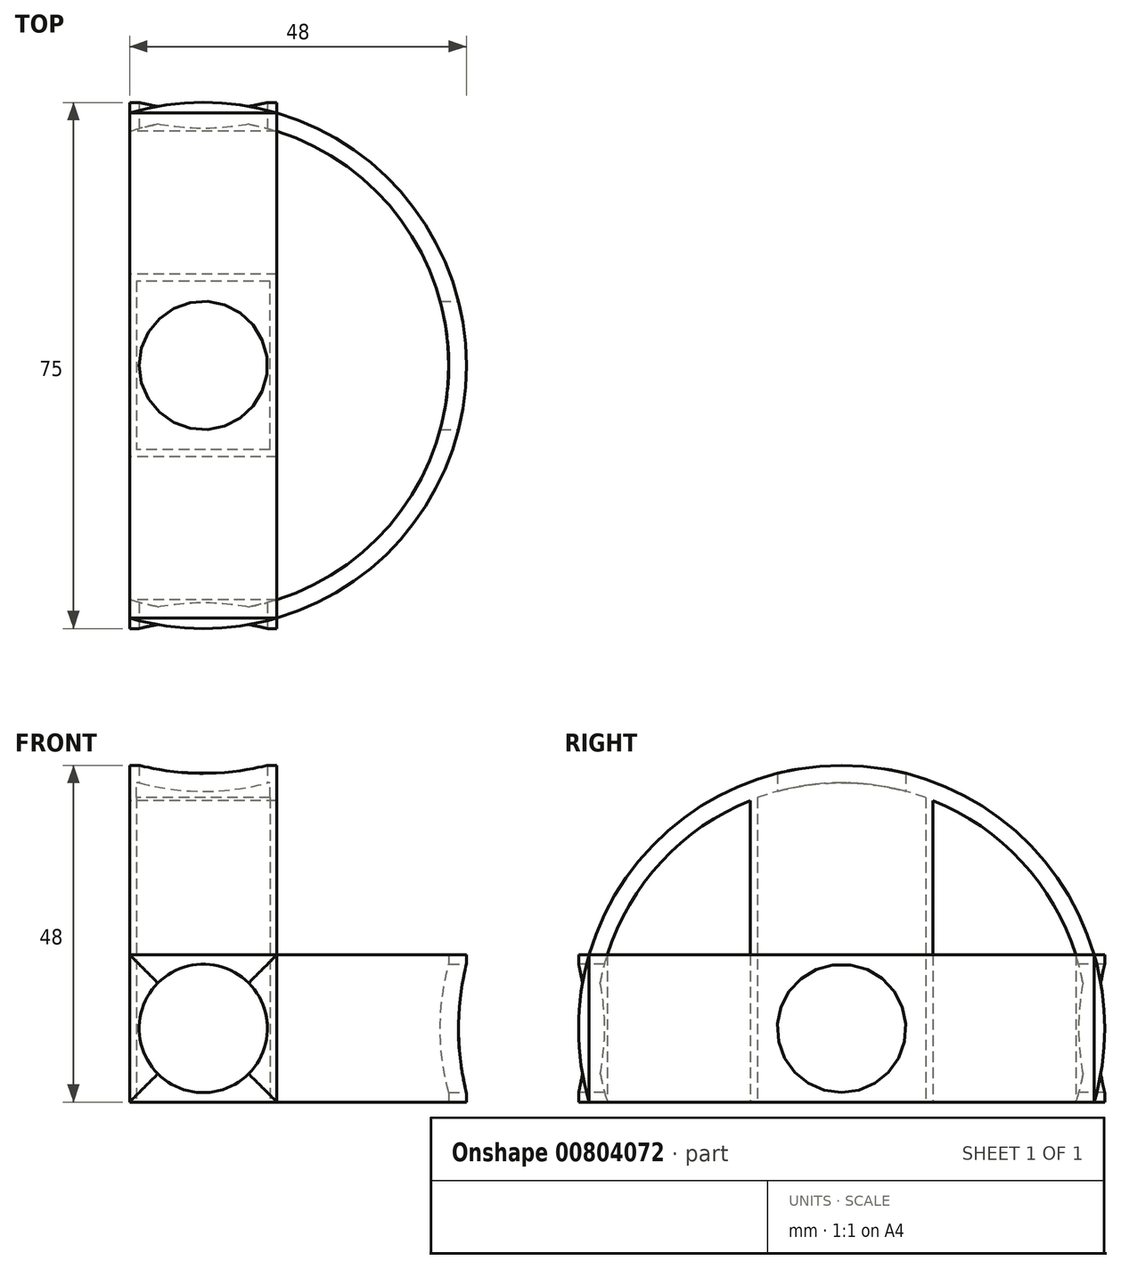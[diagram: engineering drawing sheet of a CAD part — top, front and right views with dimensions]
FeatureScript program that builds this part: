
annotation { "Feature Type Name" : "Feature", "Feature Type Description" : "" }
export const myFeature = defineFeature(function(context is Context, id is Id, definition is map)
    precondition{}
    {
        {
            var Q0;
            Q0=qCreatedBy(makeId("Top.planeOp"),FACE);
            var sketch = newSketch(context, id + "F0", { "sketchPlane" : qUnion([Q0])});
            skCircle(sketch, "E0", {"center": v(0, 0) * mm, "radius": 37.5 * mm});
            skCircle(sketch, "E1", {"center": v(0, 0) * mm, "radius": 35 * mm});
            skSolve(sketch);
        }
        {
            var Q0;
            Q0 = qSketchRegion(id + "F0", true);
            extrude(context, id + "F1", {"entities" : qUnion([Q0]), "endBound" : BoundingType.SYMMETRIC, "depth" : 21 * mm, "offsetDistance" : 25 * mm});
        }
        {
            var Q0;
            Q0=qCreatedBy(makeId("Right.planeOp"),FACE);
            var sketch = newSketch(context, id + "F2", { "sketchPlane" : qUnion([Q0])});
            skCircle(sketch, "E2", {"center": v(0, 0) * mm, "radius": 9.15 * mm});
            skSolve(sketch);
        }
        {
            var Q0;
            Q0 = qSketchRegion(id + "F2", true);
            extrude(context, id + "F3", {"entities" : qUnion([Q0]), "operationType" : NewBodyOperationType.REMOVE, "endBound" : BoundingType.SYMMETRIC, "oppositeDirection" : true, "depth" : 75 * mm, "offsetDistance" : 25 * mm});
        }
        {
            var Q0;
            Q0=qCreatedBy(makeId("Front.planeOp"),FACE);
            var sketch = newSketch(context, id + "F4", { "sketchPlane" : qUnion([Q0])});
            skCircle(sketch, "E3", {"center": v(0, 0) * mm, "radius": 9.15 * mm});
            skSolve(sketch);
        }
        {
            var Q0;
            Q0=qCreatedBy(makeId("Right.planeOp"),FACE);
            var sketch = newSketch(context, id + "F5", { "sketchPlane" : qUnion([Q0])});
            skCircle(sketch, "E4", {"center": v(0, 0) * mm, "radius": 37.5 * mm});
            skCircle(sketch, "E5", {"center": v(0, 0) * mm, "radius": 35 * mm});
            skSolve(sketch);
        }
        {
            var Q0;
            Q0 = qSketchRegion(id + "F5", true);
            extrude(context, id + "F6", {"entities" : qUnion([Q0]), "operationType" : NewBodyOperationType.ADD, "endBound" : BoundingType.SYMMETRIC, "depth" : 21 * mm, "offsetDistance" : 25 * mm});
        }
        {
            var Q0;
            Q0 = qSketchRegion(id + "F4", true);
            extrude(context, id + "F7", {"entities" : qUnion([Q0]), "operationType" : NewBodyOperationType.REMOVE, "endBound" : BoundingType.SYMMETRIC, "oppositeDirection" : true, "depth" : 75 * mm, "offsetDistance" : 25 * mm});
        }
        {
            var Q0;
            Q0=qCreatedBy(makeId("Top.planeOp"),FACE);
            var sketch = newSketch(context, id + "F8", { "sketchPlane" : qUnion([Q0])});
            skCircle(sketch, "E6", {"center": v(0, 0) * mm, "radius": 9.15 * mm});
            skSolve(sketch);
        }
        {
            var Q0;
            Q0 = qSketchRegion(id + "F8", true);
            extrude(context, id + "F9", {"entities" : qUnion([Q0]), "operationType" : NewBodyOperationType.REMOVE, "endBound" : BoundingType.SYMMETRIC, "depth" : 75 * mm, "offsetDistance" : 25 * mm});
        }
        {
            var Q0;
            Q0=qCreatedBy(makeId("Front.planeOp"),FACE);
            var sketch = newSketch(context, id + "F10", { "sketchPlane" : qUnion([Q0])});
            skLineSegment(sketch, "E7.0", {"start": v(-10.5, 10.5) * mm, "end": v(-10.5, -10.5) * mm});
            skLineSegment(sketch, "E8.0", {"start": v(-10.5, -10.5) * mm, "end": v(10.5, -10.5) * mm});
            skLineSegment(sketch, "E9", {"start": v(10.5, -10.5) * mm, "end": v(10.5, -42.37) * mm});
            skLineSegment(sketch, "E10", {"start": v(10.5, -42.37) * mm, "end": v(-13.83, -42.37) * mm});
            skLineSegment(sketch, "E11", {"start": v(-13.83, -42.37) * mm, "end": v(-13.83, -11.8) * mm});
            skLineSegment(sketch, "E12", {"start": v(-13.83, -11.8) * mm, "end": v(-41.36, -11.8) * mm});
            skLineSegment(sketch, "E13", {"start": v(-41.36, -11.8) * mm, "end": v(-41.36, 10.5) * mm});
            skLineSegment(sketch, "E14", {"start": v(-10.5, 10.5) * mm, "end": v(-41.36, 10.5) * mm});
            skSolve(sketch);
        }
        {
            var Q0;
            Q0 = qSketchRegion(id + "F10", true);
            extrude(context, id + "F11", {"entities" : qUnion([Q0]), "operationType" : NewBodyOperationType.REMOVE, "endBound" : BoundingType.SYMMETRIC, "oppositeDirection" : true, "depth" : 75 * mm, "offsetDistance" : 25 * mm});
        }
        {
            var Q0;
            Q0=qCreatedBy(makeId("Top.planeOp"),FACE);
            var sketch = newSketch(context, id + "F12", { "sketchPlane" : qUnion([Q0])});
            skLineSegment(sketch, "E15.0", {"start": v(-10.5, 13) * mm, "end": v(-10.5, -13) * mm});
            skLineSegment(sketch, "E16.0", {"start": v(10.5, 13) * mm, "end": v(10.5, -13) * mm});
            skLineSegment(sketch, "E17", {"start": v(10.5, -13) * mm, "end": v(-10.5, -13) * mm});
            skLineSegment(sketch, "E18", {"start": v(-10.5, 13) * mm, "end": v(10.5, 13) * mm});
            skLineSegment(sketch, "E19", {"start": v(9.5, 0) * mm, "end": v(9.5, 13) * mm});
            skPoint(sketch, "E19.startSnap0", {"position": v(10.5, 0) * mm});
            skLineSegment(sketch, "E20", {"start": v(9.5, 0) * mm, "end": v(9.5, -13) * mm});
            skPoint(sketch, "E21.orphan", {"position": v(10.5, -36) * mm});
            skLineSegment(sketch, "E22", {"start": v(-9.5, 13) * mm, "end": v(-9.5, -13) * mm});
            skLineSegment(sketch, "E23", {"start": v(-9.5, -12) * mm, "end": v(9.5, -12) * mm});
            skLineSegment(sketch, "E24", {"start": v(9.5, 12) * mm, "end": v(-9.5, 12) * mm});
            skPoint(sketch, "E25.orphan", {"position": v(10.5, 36) * mm});
            skSolve(sketch);
        }
        {
            var Q0;
            Q0 = qSketchRegion(id + "F12", true);
            extrude(context, id + "F13", {"entities" : qUnion([Q0]), "operationType" : NewBodyOperationType.ADD, "depth" : 35 * mm, "offsetDistance" : 25 * mm, "hasSecondDirection" : true, "secondDirectionOppositeDirection" : true, "secondDirectionDepth" : 10.5 * mm});
        }
    });
